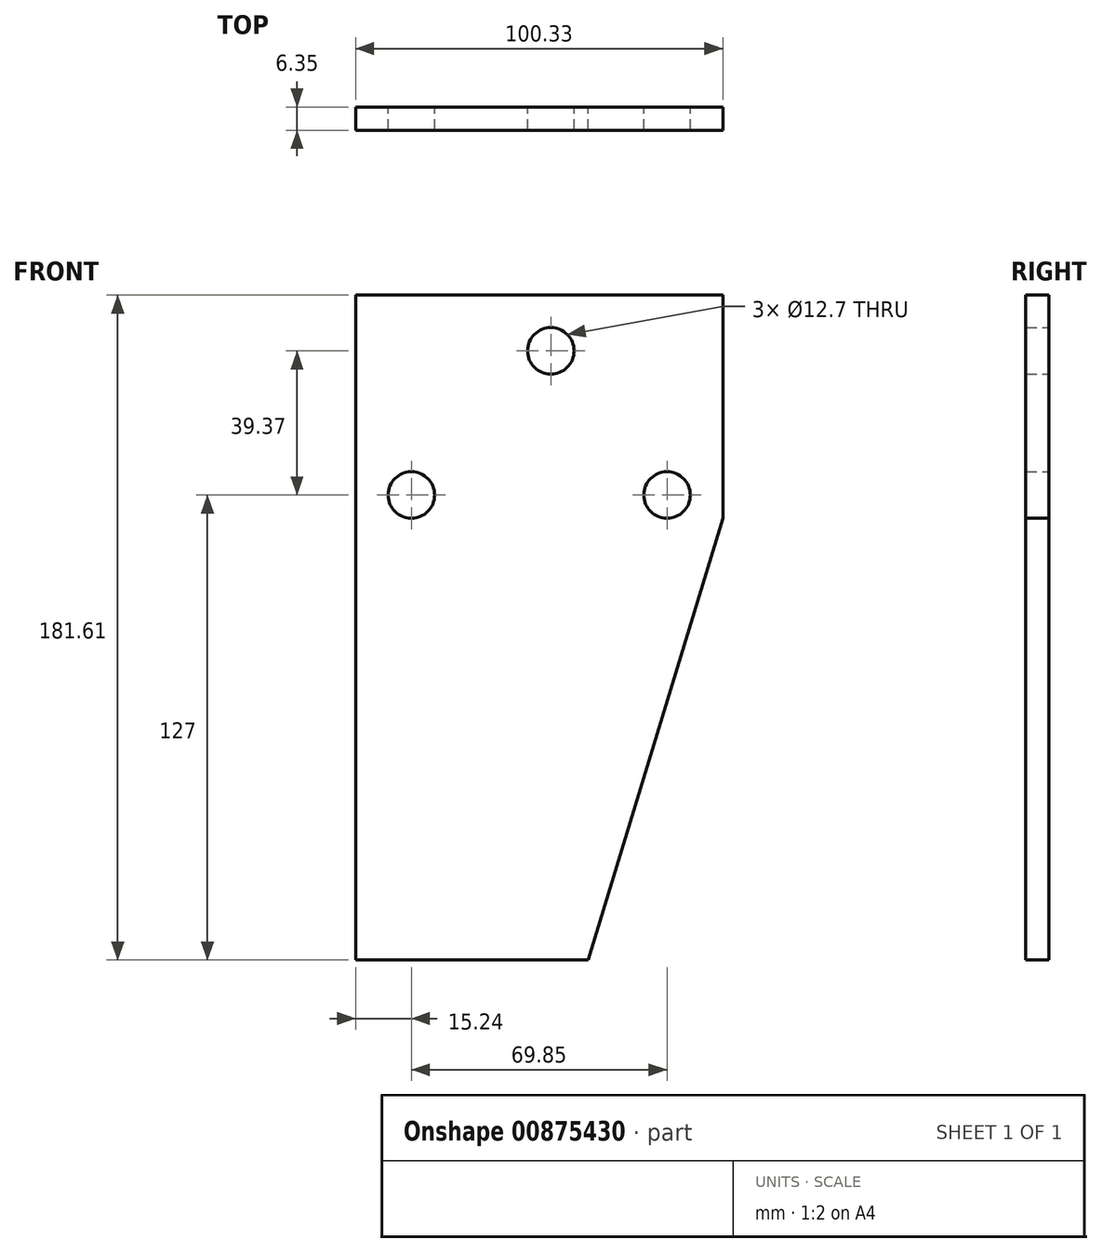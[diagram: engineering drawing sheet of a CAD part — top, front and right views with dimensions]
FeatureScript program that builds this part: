
annotation { "Feature Type Name" : "Feature", "Feature Type Description" : "" }
export const myFeature = defineFeature(function(context is Context, id is Id, definition is map)
    precondition{}
    {
        {
            var Q0;
            Q0=qCreatedBy(makeId("Front.planeOp"),FACE);
            var sketch = newSketch(context, id + "F0", { "sketchPlane" : qUnion([Q0])});
            skPoint(sketch, "E0.middle", {"position": v(0, 0) * mm});
            skLineSegment(sketch, "E1.bottom", {"start": v(31.75, 31.75) * mm, "end": v(-31.75, 31.75) * mm});
            skLineSegment(sketch, "E1.top", {"start": v(31.75, -31.75) * mm, "end": v(-31.75, -31.75) * mm});
            skLineSegment(sketch, "E1.left", {"start": v(31.75, 31.75) * mm, "end": v(31.75, -31.75) * mm});
            skLineSegment(sketch, "E1.right", {"start": v(-31.75, 31.75) * mm, "end": v(-31.75, -31.75) * mm});
            skCircle(sketch, "E2", {"center": v(31.75, 95.25) * mm, "radius": 6.35 * mm});
            skCircle(sketch, "E3", {"center": v(-38.1, 95.25) * mm, "radius": 6.35 * mm});
            skCircle(sketch, "E4", {"center": v(0, 134.62) * mm, "radius": 6.35 * mm});
            skLineSegment(sketch, "E5.bottom", {"start": v(46.99, 31.75) * mm, "end": v(-53.34, 31.75) * mm});
            skLineSegment(sketch, "E5.top", {"start": v(46.99, 149.86) * mm, "end": v(-53.34, 149.86) * mm});
            skLineSegment(sketch, "E5.left", {"start": v(46.99, 31.75) * mm, "end": v(46.99, 149.86) * mm});
            skLineSegment(sketch, "E5.right", {"start": v(-53.34, 31.75) * mm, "end": v(-53.34, 149.86) * mm});
            skLineSegment(sketch, "E6", {"start": v(-53.34, 95.25) * mm, "end": v(-31.75, 31.75) * mm});
            skLineSegment(sketch, "E7", {"start": v(-53.34, 31.75) * mm, "end": v(-53.34, -31.75) * mm});
            skLineSegment(sketch, "E8", {"start": v(-53.34, -31.75) * mm, "end": v(-31.75, -31.75) * mm});
            skLineSegment(sketch, "E9.bottom", {"start": v(-2.54, 19.05) * mm, "end": v(-40.64, 19.05) * mm, "construction": true});
            skLineSegment(sketch, "E9.top", {"start": v(-2.54, -19.05) * mm, "end": v(-40.64, -19.05) * mm, "construction": true});
            skLineSegment(sketch, "E9.left", {"start": v(-2.54, 19.05) * mm, "end": v(-2.54, -19.05) * mm, "construction": true});
            skLineSegment(sketch, "E9.right", {"start": v(-40.64, 19.05) * mm, "end": v(-40.64, -19.05) * mm, "construction": true});
            skPoint(sketch, "E9.middle", {"position": v(-21.6, 0) * mm});
            skLineSegment(sketch, "E10.bottom", {"start": v(-53.34, -31.75) * mm, "end": v(10.16, -31.75) * mm});
            skLineSegment(sketch, "E10.top", {"start": v(-53.34, 31.75) * mm, "end": v(10.16, 31.75) * mm});
            skLineSegment(sketch, "E10.left", {"start": v(-53.34, -31.75) * mm, "end": v(-53.34, 31.75) * mm});
            skLineSegment(sketch, "E10.right", {"start": v(10.16, -31.75) * mm, "end": v(10.16, 31.75) * mm});
            skLineSegment(sketch, "E11", {"start": v(80.33, 88.9) * mm, "end": v(9.6, 88.9) * mm});
            skLineSegment(sketch, "E12", {"start": v(46.99, 88.9) * mm, "end": v(10.16, -31.75) * mm});
            skSolve(sketch);
        }
        {
            var Q0;
            Q0=makeQuery(id+"F0.imprint","IMPRINT",FACE,{"disambiguationData":[TD([[makeQuery(id+"F0.imprint","IMPRINT",EDGE,{"derivedFrom":sQuery(id+"F0.wireOp",EDGE,"E2")}),-1.0]])]});
            var Q1;
            {var subQ0=sQuery(id+"F0.wireOp",EDGE,"E10.right");Q1=makeQuery(id+"F0.imprint","IMPRINT",FACE,{"disambiguationData":[TD([[makeQuery(id+"F0.imprint","IMPRINT",EDGE,{"derivedFrom":subQ0}),-1.0]])]});}
            var Q2;
            {var subQ0=sQuery(id+"F0.wireOp",EDGE,"E1.right");Q2=makeQuery(id+"F0.imprint","IMPRINT",FACE,{"disambiguationData":[TD([[makeQuery(id+"F0.imprint","IMPRINT",EDGE,{"derivedFrom":subQ0}),1.0]])]});}
            var Q3;
            {var subQ3=sQuery(id+"F0.wireOp",EDGE,"E6");Q3=makeQuery(id+"F0.imprint","IMPRINT",FACE,{"disambiguationData":[TD([[makeQuery(id+"F0.imprint","IMPRINT",EDGE,{"derivedFrom":subQ3}),-1.0]])]});}
            var Q4;
            {var subQ0=sQuery(id+"F0.wireOp",EDGE,"E1.right");Q4=makeQuery(id+"F0.imprint","IMPRINT",FACE,{"disambiguationData":[TD([[makeQuery(id+"F0.imprint","IMPRINT",EDGE,{"derivedFrom":subQ0}),-1.0]])]});}
            extrude(context, id + "F1", {"entities" : qUnion([Q0, Q1, Q2, Q3, Q4]), "depth" : 6.35 * mm, "offsetDistance" : 25.4 * mm});
        }
    });
